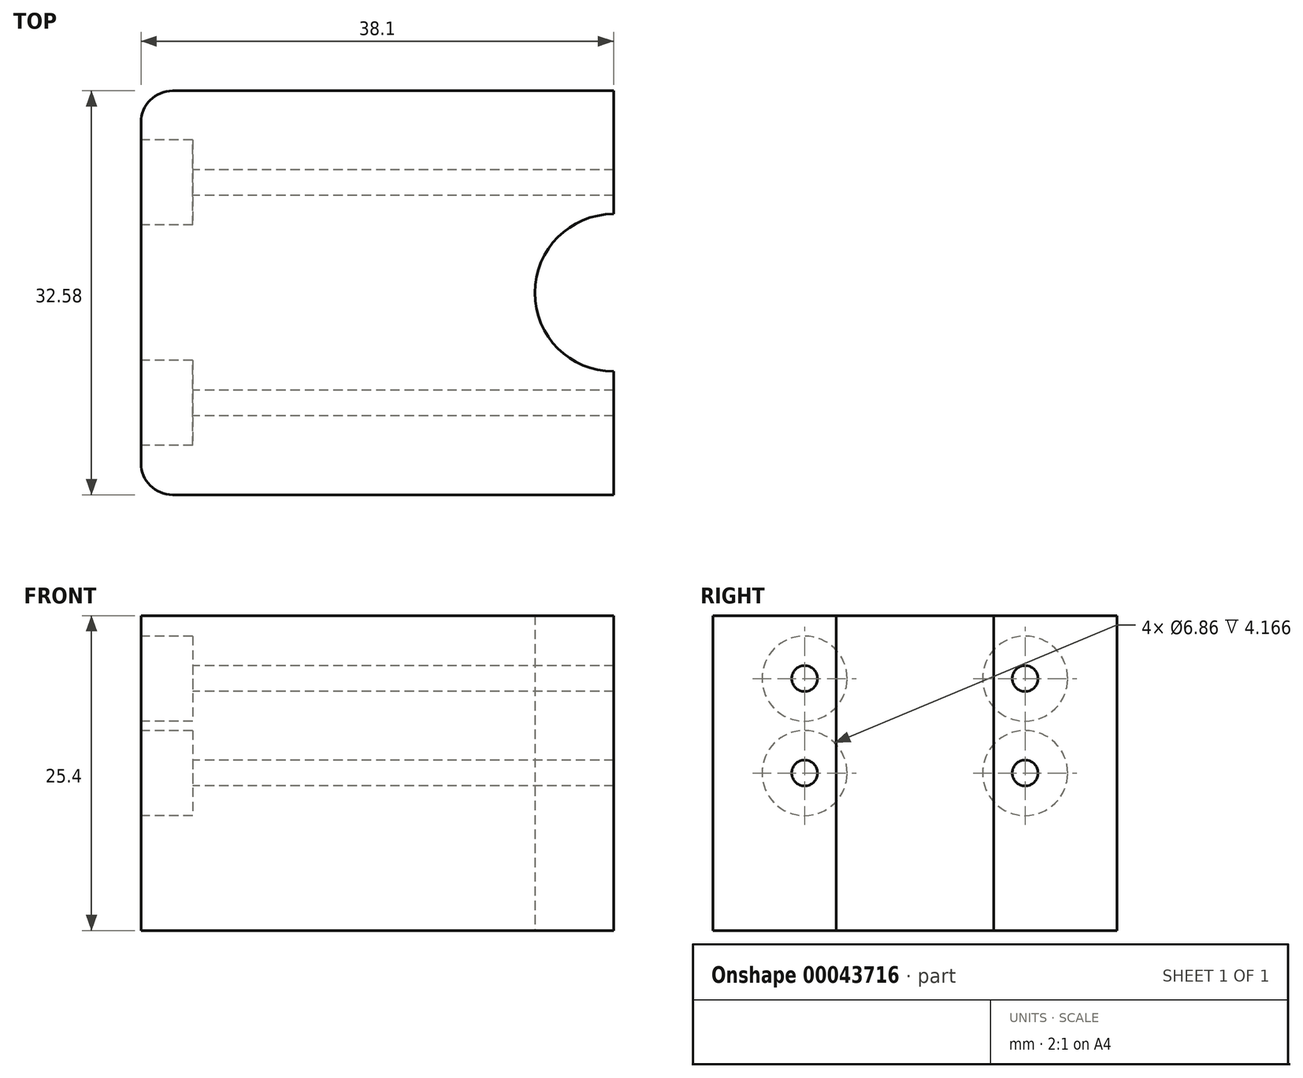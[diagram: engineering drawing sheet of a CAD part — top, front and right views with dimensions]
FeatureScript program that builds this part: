
annotation { "Feature Type Name" : "Feature", "Feature Type Description" : "" }
export const myFeature = defineFeature(function(context is Context, id is Id, definition is map)
    precondition{}
    {
        {
            var Q0;
            Q0=qCreatedBy(makeId("Top.planeOp"),FACE);
            var sketch = newSketch(context, id + "F0", { "sketchPlane" : qUnion([Q0])});
            skLineSegment(sketch, "E0.rect.bottom", {"start": v(19.05, -16.3) * mm, "end": v(-16.51, -16.3) * mm});
            skLineSegment(sketch, "E0.rect.top", {"start": v(19.05, 16.3) * mm, "end": v(-16.51, 16.3) * mm});
            skLineSegment(sketch, "E0.rect.left", {"start": v(19.05, -16.3) * mm, "end": v(19.05, -6.35) * mm});
            skLineSegment(sketch, "E0.rect.right", {"start": v(-19.05, -13.75) * mm, "end": v(-19.05, 13.75) * mm});
            skPoint(sketch, "E0.rect.middle", {"position": v(0, 0) * mm});
            skLineSegment(sketch, "E1", {"start": v(-19.05, 0) * mm, "end": v(19.05, 0) * mm, "construction": true});
            skArc(sketch, "E2", {"start": v(19.05, 6.35) * mm, "mid": v(12.7, 0) * mm, "end": v(19.05, -6.35) * mm});
            skPoint(sketch, "E3.visualSharp", {"position": v(-19.05, 16.3) * mm});
            skArc(sketch, "E3.filletArc", {"start": v(-16.51, 16.3) * mm, "mid": v(-18.3, 15.55) * mm, "end": v(-19.05, 13.75) * mm});
            skPoint(sketch, "E4.visualSharp", {"position": v(-19.05, -16.3) * mm});
            skArc(sketch, "E4.filletArc", {"start": v(-19.05, -13.75) * mm, "mid": v(-18.3, -15.55) * mm, "end": v(-16.51, -16.3) * mm});
            skLineSegment(sketch, "E5.trimOffspring", {"start": v(19.05, 6.35) * mm, "end": v(19.05, 16.3) * mm});
            skSolve(sketch);
        }
        {
            var Q0;
            Q0=makeQuery(id+"F0.imprint","IMPRINT",FACE,{"disambiguationData":[TD([[makeQuery(id+"F0.imprint","IMPRINT",EDGE,{"derivedFrom":sQuery(id+"F0.wireOp",EDGE,"E0.rect.bottom")}),-1.0]])]});
            extrude(context, id + "F1", {"entities" : qUnion([Q0]), "depth" : 25.4 * mm});
        }
        {
            var Q0;
            Q0=makeQuery(id+"F1.opExtrude","SWEPT_FACE",FACE,{"disambiguationData":[OSD([sQuery(id+"F0.wireOp",EDGE,"E0.rect.right")])]});
            var sketch = newSketch(context, id + "F2", { "sketchPlane" : qUnion([Q0])});
            skLineSegment(sketch, "E6", {"start": v(0, 25.4) * mm, "end": v(0, 0) * mm, "construction": true});
            skLineSegment(sketch, "E7", {"start": v(-13.75, 12.7) * mm, "end": v(13.75, 12.7) * mm, "construction": true});
            skCircle(sketch, "E8", {"center": v(-8.89, 20.32) * mm, "radius": 1.04 * mm});
            skCircle(sketch, "E9.MirrorC", {"center": v(8.9, 20.32) * mm, "radius": 1.04 * mm});
            skCircle(sketch, "E10", {"center": v(-8.89, 12.7) * mm, "radius": 1.04 * mm});
            skLineSegment(sketch, "E11", {"start": v(8.9, 20.32) * mm, "end": v(8.9, 0) * mm, "construction": true});
            skLineSegment(sketch, "E12", {"start": v(-8.89, 20.32) * mm, "end": v(-8.89, 0) * mm, "construction": true});
            skCircle(sketch, "E13.MirrorC", {"center": v(8.89, 12.7) * mm, "radius": 1.04 * mm});
            skSolve(sketch);
        }
        {
            var Q0;
            Q0=sQuery(id+"F2.wireOp",VERTEX,"E12.start");
            var Q1;
            Q1=sQuery(id+"F2.wireOp",VERTEX,"E10.center");
            var Q2;
            Q2=sQuery(id+"F2.wireOp",VERTEX,"E11.start");
            var Q3;
            Q3=sQuery(id+"F2.wireOp",VERTEX,"E13.MirrorC.center");
            var Q4;
            Q4=makeQuery(id+"F1.opExtrude","SWEPT_BODY",BODY,{"disambiguationData":[OSD([sQuery(id+"F0.wireOp",EDGE,"E0.rect.bottom"),sQuery(id+"F0.wireOp",EDGE,"E0.rect.top"),sQuery(id+"F0.wireOp",EDGE,"E0.rect.left"),sQuery(id+"F0.wireOp",EDGE,"E0.rect.right"),sQuery(id+"F0.wireOp",EDGE,"E2"),sQuery(id+"F0.wireOp",EDGE,"E3.filletArc"),sQuery(id+"F0.wireOp",EDGE,"E4.filletArc"),sQuery(id+"F0.wireOp",EDGE,"E5.trimOffspring")])]});
            hole(context, id + "F3", {"style" : HoleStyle.C_BORE, "holeDiameter" : 2.08 * mm, "cBoreDiameter" : 6.86 * mm, "cBoreDepth" : 4.17 * mm, "endStyle" : HoleEndStyle.THROUGH, "locations" : qUnion([Q0, Q1, Q2, Q3]), "scope" : qUnion([Q4])});
        }
    });
